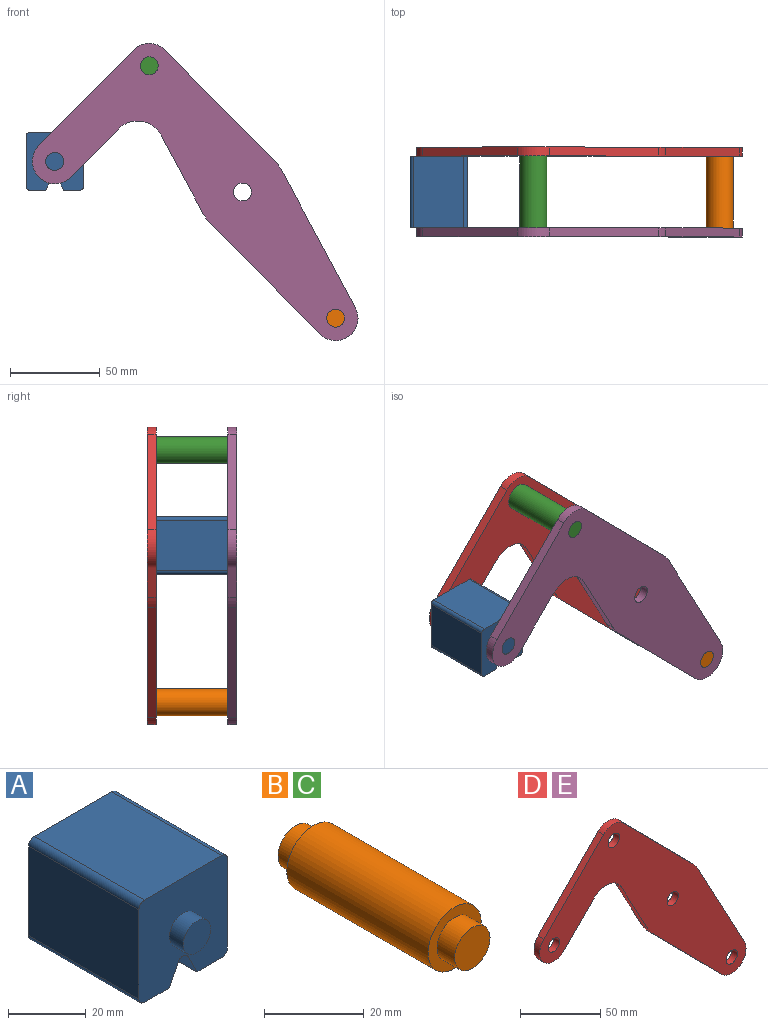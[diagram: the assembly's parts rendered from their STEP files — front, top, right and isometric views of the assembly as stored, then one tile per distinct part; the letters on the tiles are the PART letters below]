
ASSEMBLY  parts=5 mates=3
PART A: 18 faces, bbox 32.1x50x32.1 mm
  f0: plane 40x28.08mm, normal (1,0,0), area 1123.1mm2, adj f4,f10,f13,f14
  f1: plane 40x9.04mm, normal (0,0,-1), area 361.6mm2, adj f2,f4,f10,f14
  f2: plane 40x6.42mm, normal (-0.89,0,-0.45), area 287.2mm2, adj f1,f4,f10,f15
  f3: plane 40x6.42mm, normal (0.89,0,-0.45), area 287.2mm2, adj f4,f5,f10,f15
  f4: plane 32.08x32.08mm, normal (0,-1,0), area 900.6mm2, adj f0,f1,f2,f3,f5,f6,f7,f9
  f5: plane 40x9.04mm, normal (0,0,-1), area 361.6mm2, adj f3,f4,f10,f16
  f6: plane 40x28.08mm, normal (0,0,1), area 1123.1mm2, adj f4,f10,f13,f17
  f7: plane 40x28.08mm, normal (-1,0,0), area 1123.1mm2, adj f4,f10,f16,f17
  f8: plane 10x10mm, normal (0,-1,0), area 78.5mm2, adj f9
  f9: cylinder r=5mm len=10mm, axis (0,1,0), area 157.1mm2, adj f4,f8
  f10: plane 32.08x32.08mm, normal (0,1,0), area 900.6mm2, adj f0,f1,f2,f3,f5,f6,f7,f12
  f11: plane 10x10mm, normal (0,1,0), area 78.5mm2, adj f12
  f12: cylinder r=5mm len=10mm, axis (0,-1,0), area 157.1mm2, adj f10,f11
  f13: cylinder r=2mm len=40mm, axis (0,1,0), area 125.7mm2, adj f0,f4,f6,f10
  f14: cylinder r=2mm len=40mm, axis (0,-1,0), area 125.7mm2, adj f0,f1,f4,f10
  f15: cylinder r=2mm len=40mm, axis (0,1,0), area 177.1mm2, adj f2,f3,f4,f10
  f16: cylinder r=2mm len=40mm, axis (0,1,0), area 125.7mm2, adj f4,f5,f7,f10
  f17: cylinder r=2mm len=40mm, axis (0,-1,0), area 125.7mm2, adj f4,f6,f7,f10
PART B: 7 faces, bbox 15x50x15 mm
  f0: cylinder r=7.5mm len=40mm, axis (0,-1,0), area 1885mm2, adj f2,f5
  f1: cylinder r=5mm len=10mm, axis (0,1,0), area 157.1mm2, adj f2,f3
  f2: plane 15x15mm, normal (0,-1,0), area 98.2mm2, adj f0,f1
  f3: plane 10x10mm, normal (0,-1,0), area 78.5mm2, adj f1
  f4: cylinder r=5mm len=10mm, axis (0,-1,0), area 157.1mm2, adj f5,f6
  f5: plane 15x15mm, normal (0,1,0), area 98.2mm2, adj f0,f4
  f6: plane 10x10mm, normal (0,1,0), area 78.5mm2, adj f4
PART C: same geometry as B
PART D: 18 faces, bbox 181.7x5x165.8 mm
  f0: plane 43.49x23.35mm, normal (-0.88,0,-0.47), area 246.8mm2, adj f1,f14,f16,f17
  f1: cylinder r=25mm len=5.75mm, axis (0,1,0), area 35.8mm2, adj f0,f2,f16,f17
  f2: plane 61.6x60.87mm, normal (-0.71,0,-0.7), area 433mm2, adj f1,f3,f16,f17
  f3: cylinder r=12.5mm len=21.39mm, axis (0,1,0), area 178.4mm2, adj f2,f4,f16,f17
  f4: plane 76.3x40.96mm, normal (0.88,0,0.47), area 433mm2, adj f3,f5,f16,f17
  f5: cylinder r=25mm len=5.75mm, axis (0,1,0), area 35.8mm2, adj f4,f6,f16,f17
  f6: plane 61.6x60.87mm, normal (0.71,0,0.7), area 433mm2, adj f5,f7,f16,f17
  f7: cylinder r=12.5mm len=17.78mm, axis (0,1,0), area 98.9mm2, adj f6,f8,f16,f17
  f8: plane 53.35x52.71mm, normal (-0.71,0,0.7), area 375mm2, adj f7,f9,f16,f17
  f9: cylinder r=12.5mm len=21.39mm, axis (0,1,0), area 196.3mm2, adj f8,f10,f16,f17
  f10: plane 26.86x26.54mm, normal (0.71,0,-0.7), area 188.8mm2, adj f9,f14,f16,f17
  f11: cylinder r=5mm len=10mm, axis (0,1,0), area 157.1mm2, adj f16,f17
  f12: cylinder r=5mm len=10mm, axis (0,1,0), area 157.1mm2, adj f16,f17
  f13: cylinder r=5mm len=10mm, axis (0,1,0), area 157.1mm2, adj f16,f17
  f14: cylinder r=15mm len=23.89mm, axis (0,1,0), area 140.2mm2, adj f0,f10,f16,f17
  f15: cylinder r=5mm len=10mm, axis (0,1,0), area 157.1mm2, adj f16,f17
  f16: plane 181.66x165.78mm, normal (0,-1,0), area 8710.1mm2, adj f0,f1,f2,f3,f4,f5,f6,f7
  f17: plane 181.66x165.78mm, normal (0,1,0), area 8710.1mm2, adj f0,f1,f2,f3,f4,f5,f6,f7
PART E: same geometry as D
PLACE A t=(-74.94,-73.9,49.69)mm
PLACE B t=(29.01,-73.9,-91.09)mm
PLACE C t=(-74.94,-73.9,49.69)mm
PLACE D t=(-74.94,-28.9,49.69)mm
PLACE E t=(-74.94,-73.9,49.69)mm fixed
MATE fastened B.f0 <-> D.f3  axis (0,-1,0) through (-22.97,-33.9,-20.7)mm
MATE fastened D.f9 <-> A.f9  axis (0,-1,0) through (-179.63,-33.9,66.73)mm
MATE revolute A.f9 <-> E.f9  axis (0,-1,0) through (-179.63,-78.9,66.73)mm
